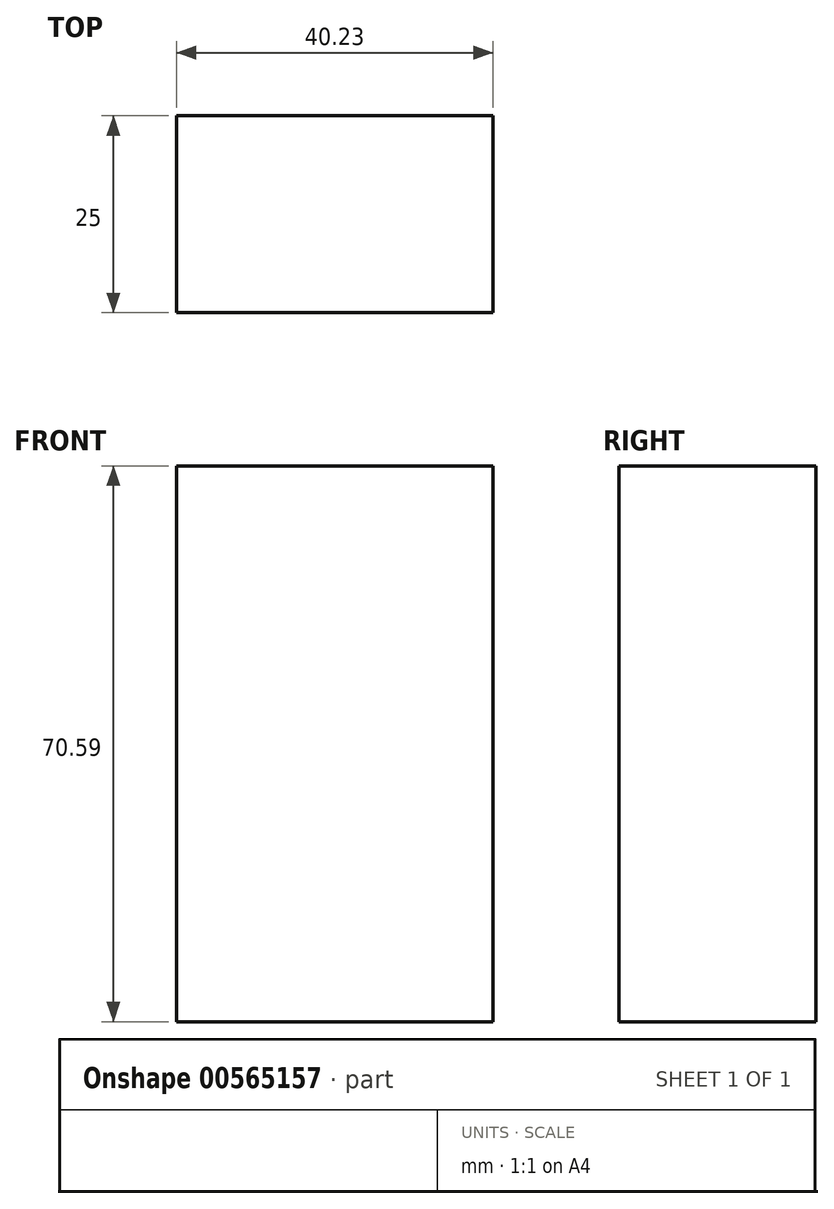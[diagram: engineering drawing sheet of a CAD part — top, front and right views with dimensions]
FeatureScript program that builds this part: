
annotation { "Feature Type Name" : "Feature", "Feature Type Description" : "" }
export const myFeature = defineFeature(function(context is Context, id is Id, definition is map)
    precondition{}
    {
        {
            var Q0;
            Q0=qCreatedBy(makeId("Front.planeOp"),FACE);
            var sketch = newSketch(context, id + "F0", { "sketchPlane" : qUnion([Q0])});
            skLineSegment(sketch, "E0.bottom", {"start": v(0, 0) * mm, "end": v(-40.23, 0) * mm});
            skLineSegment(sketch, "E0.top", {"start": v(0, 70.6) * mm, "end": v(-40.23, 70.6) * mm});
            skLineSegment(sketch, "E0.left", {"start": v(0, 0) * mm, "end": v(0, 70.6) * mm});
            skLineSegment(sketch, "E0.right", {"start": v(-40.23, 0) * mm, "end": v(-40.23, 70.6) * mm});
            skLineSegment(sketch, "E1.bottom", {"start": v(-40.23, 0) * mm, "end": v(0, 0) * mm});
            skLineSegment(sketch, "E1.left", {"start": v(-40.23, 0) * mm, "end": v(-40.23, 20.87) * mm});
            skLineSegment(sketch, "E1.right", {"start": v(0, 0) * mm, "end": v(0, 20.87) * mm});
            skSolve(sketch);
        }
        {
            var Q0;
            Q0 = qSketchRegion(id + "F0", true);
            extrude(context, id + "F1", {"entities" : qUnion([Q0]), "depth" : 25 * mm, "offsetDistance" : 25 * mm});
        }
    });
